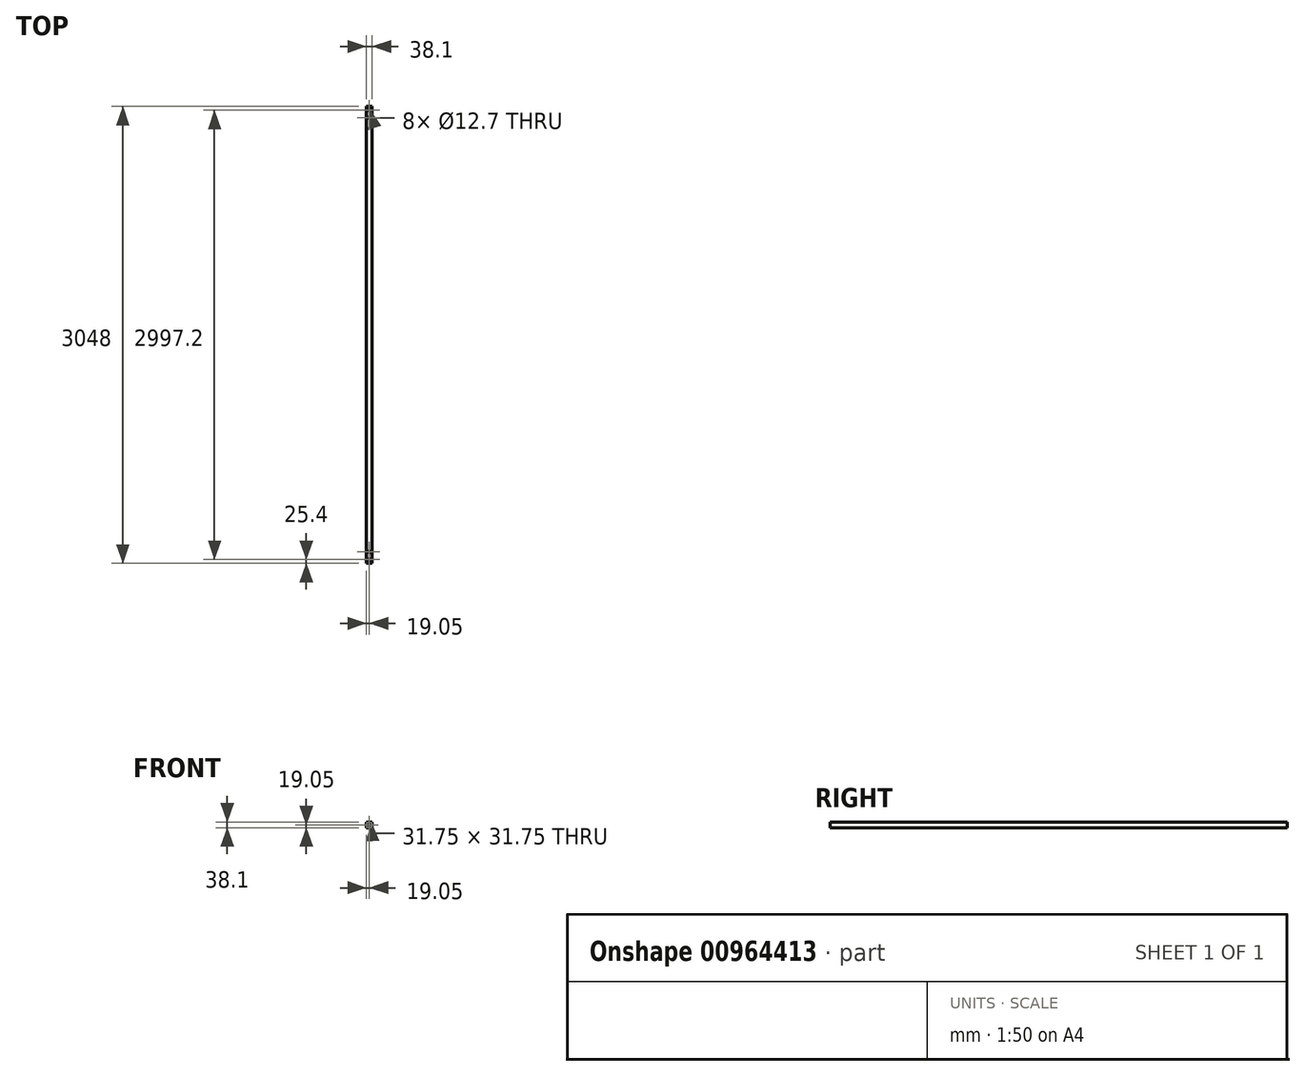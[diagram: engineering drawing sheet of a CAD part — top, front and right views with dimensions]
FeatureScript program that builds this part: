
annotation { "Feature Type Name" : "Feature", "Feature Type Description" : "" }
export const myFeature = defineFeature(function(context is Context, id is Id, definition is map)
    precondition{}
    {
        {
            var Q0;
            Q0=qCreatedBy(makeId("Front.planeOp"),FACE);
            var sketch = newSketch(context, id + "F0", { "sketchPlane" : qUnion([Q0])});
            skLineSegment(sketch, "E0.bottom", {"start": v(19.05, -19.05) * mm, "end": v(-19.05, -19.05) * mm});
            skLineSegment(sketch, "E0.top", {"start": v(19.05, 19.05) * mm, "end": v(-19.05, 19.05) * mm});
            skLineSegment(sketch, "E0.left", {"start": v(19.05, -19.05) * mm, "end": v(19.05, 19.05) * mm});
            skLineSegment(sketch, "E0.right", {"start": v(-19.05, -19.05) * mm, "end": v(-19.05, 19.05) * mm});
            skPoint(sketch, "E0.middle", {"position": v(0, 0) * mm});
            skLineSegment(sketch, "E1.bottom", {"start": v(15.88, -15.87) * mm, "end": v(-15.87, -15.88) * mm});
            skLineSegment(sketch, "E1.top", {"start": v(15.88, 15.88) * mm, "end": v(-15.88, 15.87) * mm});
            skLineSegment(sketch, "E1.left", {"start": v(15.88, -15.88) * mm, "end": v(15.88, 15.88) * mm});
            skLineSegment(sketch, "E1.right", {"start": v(-15.87, -15.88) * mm, "end": v(-15.88, 15.88) * mm});
            skSolve(sketch);
        }
        {
            var Q0;
            Q0=qSketchRegion(id+"F0",true);
            var Q1;
            Q1=qSketchRegion(id+"F2",true);
            extrude(context, id + "F1", {"entities" : qUnion([Q0, Q1]), "depth" : 3048 * mm, "offsetDistance" : 25.4 * mm});
        }
        {
            var Q0;
            Q0=makeQuery(id+"F1.opExtrude","SWEPT_FACE",FACE,{"disambiguationData":[OSD([sQuery(id+"F0.wireOp",EDGE,"E0.top")])]});
            var sketch = newSketch(context, id + "F2", { "sketchPlane" : qUnion([Q0])});
            skCircle(sketch, "E2", {"center": v(0, -25.4) * mm, "radius": 6.35 * mm});
            skCircle(sketch, "E3", {"center": v(0, -76.2) * mm, "radius": 6.35 * mm});
            skCircle(sketch, "E4", {"center": v(0, -3022.6) * mm, "radius": 6.35 * mm});
            skCircle(sketch, "E5", {"center": v(0, -2971.8) * mm, "radius": 6.35 * mm});
            skSolve(sketch);
        }
        {
            var Q0;
            Q0=qSketchRegion(id+"F2",true);
            extrude(context, id + "F3", {"entities" : qUnion([Q0]), "operationType" : NewBodyOperationType.REMOVE, "endBound" : BoundingType.THROUGH_ALL, "oppositeDirection" : true, "depth" : 25.4 * mm, "offsetDistance" : 25.4 * mm});
        }
    });
